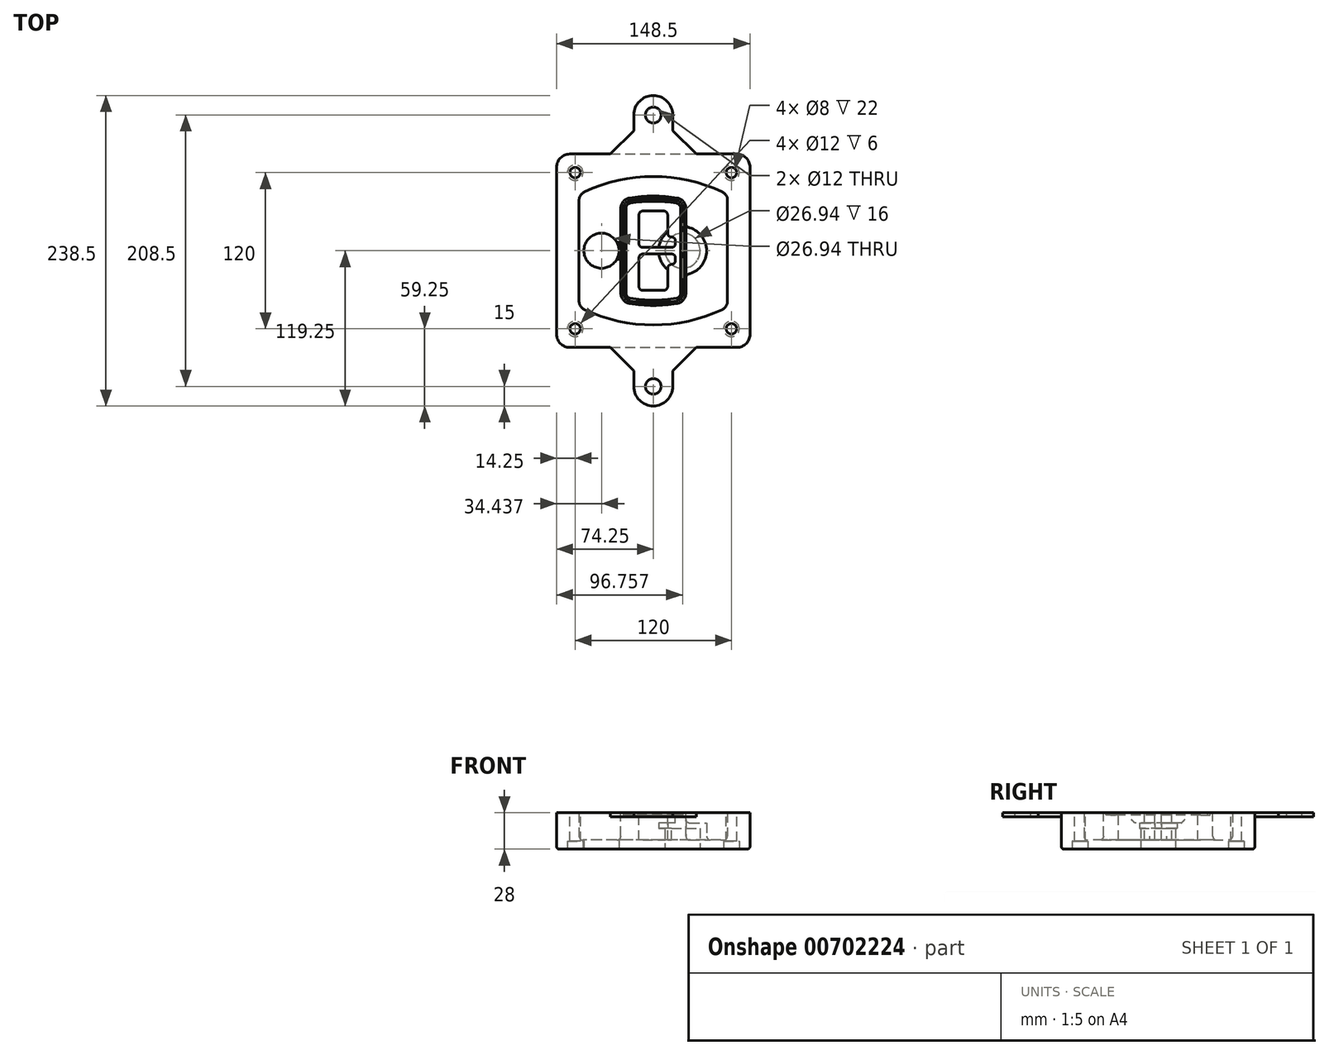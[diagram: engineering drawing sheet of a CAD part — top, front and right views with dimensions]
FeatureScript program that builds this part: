
annotation { "Feature Type Name" : "Feature", "Feature Type Description" : "" }
export const myFeature = defineFeature(function(context is Context, id is Id, definition is map)
    precondition{}
    {
        {
            var Q0;
            Q0=qCreatedBy(makeId("Top.planeOp"),FACE);
            var sketch = newSketch(context, id + "F0", { "sketchPlane" : qUnion([Q0])});
            skPoint(sketch, "E0.rect.middle", {"position": v(0, 0) * mm});
            skLineSegment(sketch, "E1.bottom", {"start": v(-64.25, -74.25) * mm, "end": v(64.25, -74.25) * mm});
            skLineSegment(sketch, "E1.top", {"start": v(-64.25, 74.25) * mm, "end": v(64.25, 74.25) * mm});
            skLineSegment(sketch, "E1.left", {"start": v(-74.25, -64.25) * mm, "end": v(-74.25, 64.25) * mm});
            skLineSegment(sketch, "E1.right", {"start": v(74.25, -64.25) * mm, "end": v(74.25, 64.25) * mm});
            skLineSegment(sketch, "E2", {"start": v(-74.25, 74.25) * mm, "end": v(74.25, -74.25) * mm, "construction": true});
            skLineSegment(sketch, "E3", {"start": v(74.25, 74.25) * mm, "end": v(-74.25, -74.25) * mm, "construction": true});
            skCircle(sketch, "E4", {"center": v(-60, 60) * mm, "radius": 4 * mm});
            skCircle(sketch, "E5", {"center": v(60, 60) * mm, "radius": 4 * mm});
            skCircle(sketch, "E6", {"center": v(60, -60) * mm, "radius": 4 * mm});
            skCircle(sketch, "E7", {"center": v(-60, -60) * mm, "radius": 4 * mm});
            skLineSegment(sketch, "E8", {"start": v(-60, 60) * mm, "end": v(60, 60) * mm, "construction": true});
            skLineSegment(sketch, "E9", {"start": v(60, 60) * mm, "end": v(60, -60) * mm, "construction": true});
            skLineSegment(sketch, "E10", {"start": v(60, -60) * mm, "end": v(-60, -60) * mm, "construction": true});
            skLineSegment(sketch, "E11", {"start": v(-60, -60) * mm, "end": v(-60, 60) * mm, "construction": true});
            skLineSegment(sketch, "E12", {"start": v(-60, 38.83) * mm, "end": v(-60, -38.83) * mm});
            skLineSegment(sketch, "E13", {"start": v(60, 38.83) * mm, "end": v(60, -38.83) * mm});
            skArc(sketch, "E14", {"start": v(54.26, 47.88) * mm, "mid": v(0, 60) * mm, "end": v(-54.26, 47.88) * mm});
            skArc(sketch, "E15", {"start": v(-54.26, -47.88) * mm, "mid": v(0, -60) * mm, "end": v(54.26, -47.88) * mm});
            skLineSegment(sketch, "E16", {"start": v(-60, 0) * mm, "end": v(60, 0) * mm, "construction": true});
            skPoint(sketch, "E17.visualSharp", {"position": v(-60, -45) * mm});
            skArc(sketch, "E17.filletArc", {"start": v(-60, -38.83) * mm, "mid": v(-58.44, -44.2) * mm, "end": v(-54.26, -47.88) * mm});
            skPoint(sketch, "E18.visualSharp", {"position": v(-60, 45) * mm});
            skArc(sketch, "E18.filletArc", {"start": v(-54.26, 47.88) * mm, "mid": v(-58.44, 44.2) * mm, "end": v(-60, 38.83) * mm});
            skPoint(sketch, "E19.visualSharp", {"position": v(60, 45) * mm});
            skArc(sketch, "E19.filletArc", {"start": v(60, 38.83) * mm, "mid": v(58.44, 44.2) * mm, "end": v(54.26, 47.88) * mm});
            skPoint(sketch, "E20.visualSharp", {"position": v(60, -45) * mm});
            skArc(sketch, "E20.filletArc", {"start": v(54.26, -47.88) * mm, "mid": v(58.44, -44.2) * mm, "end": v(60, -38.83) * mm});
            skPoint(sketch, "E21.visualSharp", {"position": v(-74.25, 74.25) * mm});
            skArc(sketch, "E21.filletArc", {"start": v(-64.25, 74.25) * mm, "mid": v(-71.32, 71.32) * mm, "end": v(-74.25, 64.25) * mm});
            skPoint(sketch, "E22.visualSharp", {"position": v(74.25, 74.25) * mm});
            skArc(sketch, "E22.filletArc", {"start": v(74.25, 64.25) * mm, "mid": v(71.32, 71.32) * mm, "end": v(64.25, 74.25) * mm});
            skPoint(sketch, "E23.visualSharp", {"position": v(74.25, -74.25) * mm});
            skArc(sketch, "E23.filletArc", {"start": v(64.25, -74.25) * mm, "mid": v(71.32, -71.32) * mm, "end": v(74.25, -64.25) * mm});
            skPoint(sketch, "E24.visualSharp", {"position": v(-74.25, -74.25) * mm});
            skArc(sketch, "E24.filletArc", {"start": v(-74.25, -64.25) * mm, "mid": v(-71.32, -71.32) * mm, "end": v(-64.25, -74.25) * mm});
            skArc(sketch, "E25.0", {"start": v(57, 38.83) * mm, "mid": v(55.9, 42.58) * mm, "end": v(52.98, 45.17) * mm});
            skLineSegment(sketch, "E25.1", {"start": v(57, 38.83) * mm, "end": v(57, -38.83) * mm});
            skArc(sketch, "E25.2", {"start": v(52.98, -45.17) * mm, "mid": v(55.9, -42.58) * mm, "end": v(57, -38.83) * mm});
            skArc(sketch, "E25.3", {"start": v(-52.98, -45.17) * mm, "mid": v(0, -57) * mm, "end": v(52.98, -45.17) * mm});
            skArc(sketch, "E25.4", {"start": v(-57, -38.83) * mm, "mid": v(-55.9, -42.58) * mm, "end": v(-52.98, -45.17) * mm});
            skArc(sketch, "E25.5", {"start": v(52.98, 45.17) * mm, "mid": v(0, 57) * mm, "end": v(-52.98, 45.17) * mm});
            skLineSegment(sketch, "E25.6", {"start": v(-57, 38.83) * mm, "end": v(-57, -38.83) * mm});
            skArc(sketch, "E25.7", {"start": v(-52.98, 45.17) * mm, "mid": v(-55.9, 42.58) * mm, "end": v(-57, 38.83) * mm});
            skArc(sketch, "E26.0", {"start": v(-55.96, 51.5) * mm, "mid": v(-61.82, 46.33) * mm, "end": v(-64, 38.83) * mm});
            skArc(sketch, "E26.1", {"start": v(55.96, 51.5) * mm, "mid": v(0, 64) * mm, "end": v(-55.96, 51.5) * mm});
            skArc(sketch, "E26.2", {"start": v(64, 38.83) * mm, "mid": v(61.82, 46.33) * mm, "end": v(55.96, 51.5) * mm});
            skLineSegment(sketch, "E26.3", {"start": v(64, 38.83) * mm, "end": v(64, -38.83) * mm});
            skArc(sketch, "E26.4", {"start": v(55.96, -51.5) * mm, "mid": v(61.82, -46.33) * mm, "end": v(64, -38.83) * mm});
            skLineSegment(sketch, "E26.5", {"start": v(-64, 38.83) * mm, "end": v(-64, -38.83) * mm});
            skArc(sketch, "E26.6", {"start": v(-55.96, -51.5) * mm, "mid": v(0, -64) * mm, "end": v(55.96, -51.5) * mm});
            skArc(sketch, "E26.7", {"start": v(-64, -38.83) * mm, "mid": v(-61.82, -46.33) * mm, "end": v(-55.96, -51.5) * mm});
            skSolve(sketch);
        }
        {
            var Q0;
            Q0=makeQuery(id+"F0.imprint","IMPRINT",FACE,{"disambiguationData":[TD([[makeQuery(id+"F0.imprint","IMPRINT",EDGE,{"derivedFrom":sQuery(id+"F0.wireOp",EDGE,"E1.bottom")}),1.0]])]});
            var Q1;
            Q1=makeQuery(id+"F0.imprint","IMPRINT",FACE,{"disambiguationData":[TD([[makeQuery(id+"F0.imprint","IMPRINT",EDGE,{"derivedFrom":sQuery(id+"F0.wireOp",EDGE,"E12")}),1.0]])]});
            var Q2;
            Q2=makeQuery(id+"F0.imprint","IMPRINT",FACE,{"disambiguationData":[TD([[makeQuery(id+"F0.imprint","IMPRINT",EDGE,{"derivedFrom":sQuery(id+"F0.wireOp",EDGE,"E25.0")}),1.0]])]});
            var Q3;
            Q3=makeQuery(id+"F0.imprint","IMPRINT",FACE,{"disambiguationData":[TD([[makeQuery(id+"F0.imprint","IMPRINT",EDGE,{"derivedFrom":sQuery(id+"F0.wireOp",EDGE,"E12")}),-1.0]])]});
            extrude(context, id + "F1", {"entities" : qUnion([Q0, Q1, Q2, Q3]), "oppositeDirection" : true, "depth" : 25 * mm});
        }
        {
            var Q0;
            Q0=makeQuery(id+"F0.imprint","IMPRINT",FACE,{"disambiguationData":[TD([[makeQuery(id+"F0.imprint","IMPRINT",EDGE,{"derivedFrom":sQuery(id+"F0.wireOp",EDGE,"E12")}),1.0]])]});
            extrude(context, id + "F2", {"entities" : qUnion([Q0]), "operationType" : NewBodyOperationType.ADD, "depth" : 3 * mm});
        }
        {
            var Q0;
            Q0=makeQuery(id+"F0.imprint","IMPRINT",FACE,{"disambiguationData":[TD([[makeQuery(id+"F0.imprint","IMPRINT",EDGE,{"derivedFrom":sQuery(id+"F0.wireOp",EDGE,"E25.0")}),1.0]])]});
            extrude(context, id + "F3", {"entities" : qUnion([Q0]), "operationType" : NewBodyOperationType.REMOVE, "oppositeDirection" : true, "depth" : 18 * mm});
        }
        {
            var Q0;
            Q0=makeQuery(id+"F2.opExtrude","CAP_FACE",FACE,{"disambiguationData":[OSD([sQuery(id+"F0.wireOp",EDGE,"E12"),sQuery(id+"F0.wireOp",EDGE,"E13"),sQuery(id+"F0.wireOp",EDGE,"E14"),sQuery(id+"F0.wireOp",EDGE,"E15"),sQuery(id+"F0.wireOp",EDGE,"E17.filletArc"),sQuery(id+"F0.wireOp",EDGE,"E18.filletArc"),sQuery(id+"F0.wireOp",EDGE,"E19.filletArc"),sQuery(id+"F0.wireOp",EDGE,"E20.filletArc"),sQuery(id+"F0.wireOp",EDGE,"E25.0"),sQuery(id+"F0.wireOp",EDGE,"E25.1"),sQuery(id+"F0.wireOp",EDGE,"E25.2"),sQuery(id+"F0.wireOp",EDGE,"E25.3"),sQuery(id+"F0.wireOp",EDGE,"E25.4"),sQuery(id+"F0.wireOp",EDGE,"E25.5"),sQuery(id+"F0.wireOp",EDGE,"E25.6"),sQuery(id+"F0.wireOp",EDGE,"E25.7")])],"isStart":false});
            var sketch = newSketch(context, id + "F4", { "sketchPlane" : qUnion([Q0])});
            skArc(sketch, "E27.0", {"start": v(-18.34, -40.45) * mm, "mid": v(0, -42) * mm, "end": v(18.34, -40.45) * mm});
            skArc(sketch, "E28.0", {"start": v(18.34, 40.45) * mm, "mid": v(0, 42) * mm, "end": v(-18.34, 40.45) * mm});
            skLineSegment(sketch, "E29", {"start": v(-25, 32.57) * mm, "end": v(-25, -32.57) * mm});
            skLineSegment(sketch, "E30", {"start": v(25, 32.57) * mm, "end": v(25, -32.57) * mm});
            skLineSegment(sketch, "E31", {"start": v(-25, 39.1) * mm, "end": v(25, 39.1) * mm, "construction": true});
            skLineSegment(sketch, "E32", {"start": v(-25, -39.1) * mm, "end": v(25, -39.1) * mm, "construction": true});
            skPoint(sketch, "E33.visualSharp", {"position": v(-25, 39.1) * mm});
            skArc(sketch, "E33.filletArc", {"start": v(-18.34, 40.45) * mm, "mid": v(-23.11, 37.73) * mm, "end": v(-25, 32.57) * mm});
            skPoint(sketch, "E34.visualSharp", {"position": v(25, 39.1) * mm});
            skArc(sketch, "E34.filletArc", {"start": v(25, 32.57) * mm, "mid": v(23.11, 37.73) * mm, "end": v(18.34, 40.45) * mm});
            skPoint(sketch, "E35.visualSharp", {"position": v(25, -39.1) * mm});
            skArc(sketch, "E35.filletArc", {"start": v(18.34, -40.45) * mm, "mid": v(23.11, -37.73) * mm, "end": v(25, -32.57) * mm});
            skPoint(sketch, "E36.visualSharp", {"position": v(-25, -39.1) * mm});
            skArc(sketch, "E36.filletArc", {"start": v(-25, -32.57) * mm, "mid": v(-23.11, -37.73) * mm, "end": v(-18.34, -40.45) * mm});
            skArc(sketch, "E37.0", {"start": v(52.98, 45.17) * mm, "mid": v(0, 57) * mm, "end": v(-52.98, 45.17) * mm});
            skArc(sketch, "E37.1", {"start": v(-52.98, 45.17) * mm, "mid": v(-55.9, 42.58) * mm, "end": v(-57, 38.83) * mm});
            skLineSegment(sketch, "E37.2", {"start": v(-57, 38.83) * mm, "end": v(-57, -38.83) * mm});
            skArc(sketch, "E37.3", {"start": v(-57, -38.83) * mm, "mid": v(-55.9, -42.58) * mm, "end": v(-52.98, -45.17) * mm});
            skArc(sketch, "E37.4", {"start": v(-52.98, -45.17) * mm, "mid": v(0, -57) * mm, "end": v(52.98, -45.17) * mm});
            skArc(sketch, "E37.5", {"start": v(52.98, -45.17) * mm, "mid": v(55.9, -42.58) * mm, "end": v(57, -38.83) * mm});
            skLineSegment(sketch, "E37.6", {"start": v(57, 38.83) * mm, "end": v(57, -38.83) * mm});
            skArc(sketch, "E37.7", {"start": v(57, 38.83) * mm, "mid": v(55.9, 42.58) * mm, "end": v(52.98, 45.17) * mm});
            skLineSegment(sketch, "E38.0", {"start": v(23, 32.57) * mm, "end": v(23, -32.57) * mm});
            skArc(sketch, "E38.1", {"start": v(18, -38.48) * mm, "mid": v(21.58, -36.44) * mm, "end": v(23, -32.57) * mm});
            skArc(sketch, "E38.2", {"start": v(-18, -38.48) * mm, "mid": v(0, -40) * mm, "end": v(18, -38.48) * mm});
            skArc(sketch, "E38.3", {"start": v(-23, -32.57) * mm, "mid": v(-21.58, -36.44) * mm, "end": v(-18, -38.48) * mm});
            skLineSegment(sketch, "E38.4", {"start": v(-23, 32.57) * mm, "end": v(-23, -32.57) * mm});
            skArc(sketch, "E38.5", {"start": v(23, 32.57) * mm, "mid": v(21.58, 36.44) * mm, "end": v(18, 38.48) * mm});
            skArc(sketch, "E38.6", {"start": v(-18, 38.48) * mm, "mid": v(-21.58, 36.44) * mm, "end": v(-23, 32.57) * mm});
            skArc(sketch, "E38.7", {"start": v(18, 38.48) * mm, "mid": v(0, 40) * mm, "end": v(-18, 38.48) * mm});
            skArc(sketch, "E39.0", {"start": v(21, 32.57) * mm, "mid": v(20.06, 35.15) * mm, "end": v(17.67, 36.5) * mm});
            skLineSegment(sketch, "E39.1", {"start": v(21, 32.57) * mm, "end": v(21, -32.57) * mm});
            skArc(sketch, "E39.2", {"start": v(17.67, -36.5) * mm, "mid": v(20.06, -35.15) * mm, "end": v(21, -32.57) * mm});
            skArc(sketch, "E39.3", {"start": v(-17.67, -36.5) * mm, "mid": v(0, -38) * mm, "end": v(17.67, -36.5) * mm});
            skArc(sketch, "E39.4", {"start": v(-21, -32.57) * mm, "mid": v(-20.06, -35.15) * mm, "end": v(-17.67, -36.5) * mm});
            skArc(sketch, "E39.5", {"start": v(17.67, 36.5) * mm, "mid": v(0, 38) * mm, "end": v(-17.67, 36.5) * mm});
            skLineSegment(sketch, "E39.6", {"start": v(-21, 32.57) * mm, "end": v(-21, -32.57) * mm});
            skArc(sketch, "E39.7", {"start": v(-17.67, 36.5) * mm, "mid": v(-20.06, 35.15) * mm, "end": v(-21, 32.57) * mm});
            skLineSegment(sketch, "E40", {"start": v(-25, 0) * mm, "end": v(25, 0) * mm, "construction": true});
            skLineSegment(sketch, "E41", {"start": v(-11, 5.5) * mm, "end": v(-11, 27.5) * mm});
            skLineSegment(sketch, "E42", {"start": v(-8, 30.5) * mm, "end": v(8, 30.5) * mm});
            skLineSegment(sketch, "E43", {"start": v(11, 27.5) * mm, "end": v(11, 13.5) * mm});
            skLineSegment(sketch, "E44", {"start": v(14, 10.5) * mm, "end": v(14, 10.5) * mm});
            skLineSegment(sketch, "E45", {"start": v(17, 7.5) * mm, "end": v(17, 5.5) * mm});
            skLineSegment(sketch, "E46", {"start": v(14, 2.5) * mm, "end": v(-8, 2.5) * mm});
            skPoint(sketch, "E47.visualSharp", {"position": v(-11, 30.5) * mm});
            skArc(sketch, "E47.filletArc", {"start": v(-8, 30.5) * mm, "mid": v(-10.12, 29.62) * mm, "end": v(-11, 27.5) * mm});
            skPoint(sketch, "E48.visualSharp", {"position": v(11, 30.5) * mm});
            skArc(sketch, "E48.filletArc", {"start": v(11, 27.5) * mm, "mid": v(10.12, 29.62) * mm, "end": v(8, 30.5) * mm});
            skPoint(sketch, "E49.visualSharp", {"position": v(11, 10.5) * mm});
            skArc(sketch, "E49.filletArc", {"start": v(11, 13.5) * mm, "mid": v(11.88, 11.38) * mm, "end": v(14, 10.5) * mm});
            skPoint(sketch, "E50.visualSharp", {"position": v(17, 10.5) * mm});
            skArc(sketch, "E50.filletArc", {"start": v(17, 7.5) * mm, "mid": v(16.12, 9.62) * mm, "end": v(14, 10.5) * mm});
            skPoint(sketch, "E51.visualSharp", {"position": v(17, 2.5) * mm});
            skArc(sketch, "E51.filletArc", {"start": v(14, 2.5) * mm, "mid": v(16.12, 3.38) * mm, "end": v(17, 5.5) * mm});
            skPoint(sketch, "E52.visualSharp", {"position": v(-11, 2.5) * mm});
            skArc(sketch, "E52.filletArc", {"start": v(-11, 5.5) * mm, "mid": v(-10.12, 3.38) * mm, "end": v(-8, 2.5) * mm});
            skLineSegment(sketch, "E53.0.MirrorCS", {"start": v(14, -2.5) * mm, "end": v(-8, -2.5) * mm});
            skArc(sketch, "E54.0.MirrorCS", {"start": v(-11, -5.5) * mm, "mid": v(-10.12, -3.38) * mm, "end": v(-8, -2.5) * mm});
            skLineSegment(sketch, "E55.0.MirrorCS", {"start": v(-11, -5.5) * mm, "end": v(-11, -27.5) * mm});
            skArc(sketch, "E56.0.MirrorCS", {"start": v(-8, -30.5) * mm, "mid": v(-10.12, -29.62) * mm, "end": v(-11, -27.5) * mm});
            skLineSegment(sketch, "E57.0.MirrorCS", {"start": v(-8, -30.5) * mm, "end": v(8, -30.5) * mm});
            skArc(sketch, "E58.0.MirrorCS", {"start": v(11, -27.5) * mm, "mid": v(10.12, -29.62) * mm, "end": v(8, -30.5) * mm});
            skLineSegment(sketch, "E59.0.MirrorCS", {"start": v(11, -27.5) * mm, "end": v(11, -13.5) * mm});
            skArc(sketch, "E60.0.MirrorCS", {"start": v(11, -13.5) * mm, "mid": v(11.88, -11.38) * mm, "end": v(14, -10.5) * mm});
            skArc(sketch, "E61.0.MirrorCS", {"start": v(17, -7.5) * mm, "mid": v(16.12, -9.62) * mm, "end": v(14, -10.5) * mm});
            skLineSegment(sketch, "E62.0.MirrorCS", {"start": v(17, -7.5) * mm, "end": v(17, -5.5) * mm});
            skArc(sketch, "E63.0.MirrorCS", {"start": v(14, -2.5) * mm, "mid": v(16.12, -3.38) * mm, "end": v(17, -5.5) * mm});
            skSolve(sketch);
        }
        {
            var Q0;
            Q0=makeQuery(id+"F4.imprint","IMPRINT",FACE,{"disambiguationData":[TD([[makeQuery(id+"F4.imprint","IMPRINT",EDGE,{"derivedFrom":sQuery(id+"F4.wireOp",EDGE,"E27.0")}),1.0]])]});
            var Q1;
            Q1=makeQuery(id+"F4.imprint","IMPRINT",FACE,{"disambiguationData":[TD([[makeQuery(id+"F4.imprint","IMPRINT",EDGE,{"derivedFrom":sQuery(id+"F4.wireOp",EDGE,"E38.0")}),-1.0]])]});
            var Q2;
            Q2=makeQuery(id+"F4.imprint","IMPRINT",FACE,{"disambiguationData":[TD([[makeQuery(id+"F4.imprint","IMPRINT",EDGE,{"derivedFrom":sQuery(id+"F4.wireOp",EDGE,"E39.0")}),1.0]])]});
            extrude(context, id + "F5", {"entities" : qUnion([Q0, Q1, Q2]), "operationType" : NewBodyOperationType.ADD, "endBound" : BoundingType.UP_TO_NEXT, "oppositeDirection" : true, "depth" : 25 * mm});
        }
        {
            var Q0;
            Q0=makeQuery(id+"F4.imprint","IMPRINT",FACE,{"disambiguationData":[TD([[makeQuery(id+"F4.imprint","IMPRINT",EDGE,{"derivedFrom":sQuery(id+"F4.wireOp",EDGE,"E38.0")}),-1.0]])]});
            extrude(context, id + "F6", {"entities" : qUnion([Q0]), "operationType" : NewBodyOperationType.REMOVE, "oppositeDirection" : true, "depth" : 2 * mm});
        }
        {
            var Q0;
            Q0=makeQuery(id+"F1.opExtrude","CAP_FACE",FACE,{"disambiguationData":[OSD([sQuery(id+"F0.wireOp",EDGE,"E1.bottom"),sQuery(id+"F0.wireOp",EDGE,"E1.top"),sQuery(id+"F0.wireOp",EDGE,"E1.left"),sQuery(id+"F0.wireOp",EDGE,"E1.right"),sQuery(id+"F0.wireOp",EDGE,"E4"),sQuery(id+"F0.wireOp",EDGE,"E5"),sQuery(id+"F0.wireOp",EDGE,"E6"),sQuery(id+"F0.wireOp",EDGE,"E7"),sQuery(id+"F0.wireOp",EDGE,"E21.filletArc"),sQuery(id+"F0.wireOp",EDGE,"E22.filletArc"),sQuery(id+"F0.wireOp",EDGE,"E23.filletArc"),sQuery(id+"F0.wireOp",EDGE,"E24.filletArc")])],"isStart":false});
            var sketch = newSketch(context, id + "F7", { "sketchPlane" : qUnion([Q0])});
            skCircle(sketch, "E64", {"center": v(22.5, 0) * mm, "radius": 13.47 * mm});
            skCircle(sketch, "E65", {"center": v(-39.81, 0) * mm, "radius": 13.47 * mm});
            skLineSegment(sketch, "E66", {"start": v(74.25, 0) * mm, "end": v(-74.25, 0) * mm});
            skCircle(sketch, "E67", {"center": v(22.5, 0) * mm, "radius": 18.47 * mm});
            skCircle(sketch, "E68", {"center": v(60, -60) * mm, "radius": 6 * mm});
            skCircle(sketch, "E69", {"center": v(-60, -60) * mm, "radius": 6 * mm});
            skCircle(sketch, "E70", {"center": v(-60, 60) * mm, "radius": 6 * mm});
            skCircle(sketch, "E71", {"center": v(60, 60) * mm, "radius": 6 * mm});
            skSolve(sketch);
        }
        {
            var Q0;
            {var subQ1=sQuery(id+"F7.wireOp",EDGE,"E66");var subQ4=sQuery(id+"F7.wireOp",EDGE,"E64");var subQ6=makeQuery(id+"F7.imprint","INTERSECT",VERTEX,{"disambiguationData":[OD(0.0)],"derivedFrom":[subQ4,subQ1]});Q0=makeQuery(id+"F7.imprint","IMPRINT",FACE,{"disambiguationData":[TD([[makeQuery(id+"F7.imprint","IMPRINT",EDGE,{"disambiguationData":[TD([[subQ6,-1.0]])],"derivedFrom":subQ4}),-1.0]])]});}
            var Q1;
            {var subQ0=sQuery(id+"F7.wireOp",EDGE,"E66");var subQ1=sQuery(id+"F7.wireOp",EDGE,"E64");var subQ3=makeQuery(id+"F7.imprint","INTERSECT",VERTEX,{"disambiguationData":[OD(0.0)],"derivedFrom":[subQ1,subQ0]});Q1=makeQuery(id+"F7.imprint","IMPRINT",FACE,{"disambiguationData":[TD([[makeQuery(id+"F7.imprint","IMPRINT",EDGE,{"disambiguationData":[TD([[subQ3,-1.0]])],"derivedFrom":subQ1}),1.0]])]});}
            var Q2;
            {var subQ0=sQuery(id+"F7.wireOp",EDGE,"E66");var subQ1=sQuery(id+"F7.wireOp",EDGE,"E64");var subQ3=makeQuery(id+"F7.imprint","INTERSECT",VERTEX,{"disambiguationData":[OD(0.0)],"derivedFrom":[subQ1,subQ0]});Q2=makeQuery(id+"F7.imprint","IMPRINT",FACE,{"disambiguationData":[TD([[makeQuery(id+"F7.imprint","IMPRINT",EDGE,{"disambiguationData":[TD([[subQ3,1.0]])],"derivedFrom":subQ1}),1.0]])]});}
            var Q3;
            {var subQ1=sQuery(id+"F7.wireOp",EDGE,"E66");var subQ4=sQuery(id+"F7.wireOp",EDGE,"E64");var subQ6=makeQuery(id+"F7.imprint","INTERSECT",VERTEX,{"disambiguationData":[OD(0.0)],"derivedFrom":[subQ4,subQ1]});Q3=makeQuery(id+"F7.imprint","IMPRINT",FACE,{"disambiguationData":[TD([[makeQuery(id+"F7.imprint","IMPRINT",EDGE,{"disambiguationData":[TD([[subQ6,1.0]])],"derivedFrom":subQ4}),-1.0]])]});}
            extrude(context, id + "F8", {"entities" : qUnion([Q0, Q1, Q2, Q3]), "operationType" : NewBodyOperationType.ADD, "oppositeDirection" : true, "depth" : 20 * mm});
        }
        {
            var Q0;
            {var subQ0=sQuery(id+"F7.wireOp",EDGE,"E66");var subQ1=sQuery(id+"F7.wireOp",EDGE,"E64");var subQ3=makeQuery(id+"F7.imprint","INTERSECT",VERTEX,{"disambiguationData":[OD(0.0)],"derivedFrom":[subQ1,subQ0]});Q0=makeQuery(id+"F7.imprint","IMPRINT",FACE,{"disambiguationData":[TD([[makeQuery(id+"F7.imprint","IMPRINT",EDGE,{"disambiguationData":[TD([[subQ3,-1.0]])],"derivedFrom":subQ1}),1.0]])]});}
            var Q1;
            {var subQ0=sQuery(id+"F7.wireOp",EDGE,"E66");var subQ1=sQuery(id+"F7.wireOp",EDGE,"E64");var subQ3=makeQuery(id+"F7.imprint","INTERSECT",VERTEX,{"disambiguationData":[OD(0.0)],"derivedFrom":[subQ1,subQ0]});Q1=makeQuery(id+"F7.imprint","IMPRINT",FACE,{"disambiguationData":[TD([[makeQuery(id+"F7.imprint","IMPRINT",EDGE,{"disambiguationData":[TD([[subQ3,1.0]])],"derivedFrom":subQ1}),1.0]])]});}
            extrude(context, id + "F9", {"entities" : qUnion([Q0, Q1]), "operationType" : NewBodyOperationType.REMOVE, "oppositeDirection" : true, "depth" : 16 * mm});
        }
        {
            var Q0;
            {var subQ0=sQuery(id+"F7.wireOp",EDGE,"E66");var subQ1=sQuery(id+"F7.wireOp",EDGE,"E65");var subQ3=makeQuery(id+"F7.imprint","INTERSECT",VERTEX,{"disambiguationData":[OD(0.0)],"derivedFrom":[subQ1,subQ0]});Q0=makeQuery(id+"F7.imprint","IMPRINT",FACE,{"disambiguationData":[TD([[makeQuery(id+"F7.imprint","IMPRINT",EDGE,{"disambiguationData":[TD([[subQ3,-1.0]])],"derivedFrom":subQ1}),1.0]])]});}
            var Q1;
            {var subQ0=sQuery(id+"F7.wireOp",EDGE,"E66");var subQ1=sQuery(id+"F7.wireOp",EDGE,"E65");var subQ3=makeQuery(id+"F7.imprint","INTERSECT",VERTEX,{"disambiguationData":[OD(0.0)],"derivedFrom":[subQ1,subQ0]});Q1=makeQuery(id+"F7.imprint","IMPRINT",FACE,{"disambiguationData":[TD([[makeQuery(id+"F7.imprint","IMPRINT",EDGE,{"disambiguationData":[TD([[subQ3,1.0]])],"derivedFrom":subQ1}),1.0]])]});}
            extrude(context, id + "F10", {"entities" : qUnion([Q0, Q1]), "operationType" : NewBodyOperationType.REMOVE, "oppositeDirection" : true, "depth" : 25 * mm});
        }
        {
            var Q0;
            Q0=makeQuery(id+"F7.imprint","IMPRINT",FACE,{"disambiguationData":[TD([[makeQuery(id+"F7.imprint","IMPRINT",EDGE,{"derivedFrom":sQuery(id+"F7.wireOp",EDGE,"E68")}),1.0]])]});
            var Q1;
            Q1=makeQuery(id+"F7.imprint","IMPRINT",FACE,{"disambiguationData":[TD([[makeQuery(id+"F7.imprint","IMPRINT",EDGE,{"derivedFrom":makeQuery(id+"F1.opExtrude","CAP_EDGE",EDGE,{"disambiguationData":[OSD([sQuery(id+"F0.wireOp",EDGE,"E5")])],"isStart":false})}),-1.0]])]});
            var Q2;
            Q2=makeQuery(id+"F7.imprint","IMPRINT",FACE,{"disambiguationData":[TD([[makeQuery(id+"F7.imprint","IMPRINT",EDGE,{"derivedFrom":sQuery(id+"F7.wireOp",EDGE,"E69")}),1.0]])]});
            var Q3;
            Q3=makeQuery(id+"F7.imprint","IMPRINT",FACE,{"disambiguationData":[TD([[makeQuery(id+"F7.imprint","IMPRINT",EDGE,{"derivedFrom":makeQuery(id+"F1.opExtrude","CAP_EDGE",EDGE,{"disambiguationData":[OSD([sQuery(id+"F0.wireOp",EDGE,"E4")])],"isStart":false})}),-1.0]])]});
            var Q4;
            Q4=makeQuery(id+"F7.imprint","IMPRINT",FACE,{"disambiguationData":[TD([[makeQuery(id+"F7.imprint","IMPRINT",EDGE,{"derivedFrom":sQuery(id+"F7.wireOp",EDGE,"E70")}),1.0]])]});
            var Q5;
            Q5=makeQuery(id+"F7.imprint","IMPRINT",FACE,{"disambiguationData":[TD([[makeQuery(id+"F7.imprint","IMPRINT",EDGE,{"derivedFrom":makeQuery(id+"F1.opExtrude","CAP_EDGE",EDGE,{"disambiguationData":[OSD([sQuery(id+"F0.wireOp",EDGE,"E7")])],"isStart":false})}),-1.0]])]});
            var Q6;
            Q6=makeQuery(id+"F7.imprint","IMPRINT",FACE,{"disambiguationData":[TD([[makeQuery(id+"F7.imprint","IMPRINT",EDGE,{"derivedFrom":sQuery(id+"F7.wireOp",EDGE,"E71")}),1.0]])]});
            var Q7;
            Q7=makeQuery(id+"F7.imprint","IMPRINT",FACE,{"disambiguationData":[TD([[makeQuery(id+"F7.imprint","IMPRINT",EDGE,{"derivedFrom":makeQuery(id+"F1.opExtrude","CAP_EDGE",EDGE,{"disambiguationData":[OSD([sQuery(id+"F0.wireOp",EDGE,"E6")])],"isStart":false})}),-1.0]])]});
            extrude(context, id + "F11", {"entities" : qUnion([Q0, Q1, Q2, Q3, Q4, Q5, Q6, Q7]), "operationType" : NewBodyOperationType.REMOVE, "oppositeDirection" : true, "depth" : 6 * mm});
        }
        {
            var Q0;
            Q0=makeQuery(id+"F9.boolean.opBoolean","COPY",FACE,{"derivedFrom":makeQuery(id+"F9.opExtrude","CAP_FACE",FACE,{"disambiguationData":[OSD([sQuery(id+"F7.wireOp",EDGE,"E64")])],"isStart":false})});
            var sketch = newSketch(context, id + "F12", { "sketchPlane" : qUnion([Q0])});
            skArc(sketch, "E72.0", {"start": v(11, 14.45) * mm, "mid": v(6.45, 9.13) * mm, "end": v(4.2, 2.5) * mm});
            skArc(sketch, "E72.1", {"start": v(4.2, -2.5) * mm, "mid": v(6.45, -9.13) * mm, "end": v(11, -14.45) * mm});
            skLineSegment(sketch, "E73", {"start": v(4.2, -2.5) * mm, "end": v(14, -2.5) * mm});
            skLineSegment(sketch, "E74.0", {"start": v(14, 2.5) * mm, "end": v(4.2, 2.5) * mm});
            skArc(sketch, "E74.1", {"start": v(14, 2.5) * mm, "mid": v(16.12, 3.38) * mm, "end": v(17, 5.5) * mm});
            skLineSegment(sketch, "E74.2", {"start": v(17, 7.5) * mm, "end": v(17, 5.5) * mm});
            skArc(sketch, "E74.3", {"start": v(17, 7.5) * mm, "mid": v(16.12, 9.62) * mm, "end": v(14, 10.5) * mm});
            skArc(sketch, "E74.4", {"start": v(11, 13.5) * mm, "mid": v(11.88, 11.38) * mm, "end": v(14, 10.5) * mm});
            skLineSegment(sketch, "E74.5", {"start": v(11, 14.45) * mm, "end": v(11, 13.5) * mm});
            skLineSegment(sketch, "E74.7", {"start": v(14, -2.5) * mm, "end": v(4.2, -2.5) * mm});
            skArc(sketch, "E74.8", {"start": v(14, -2.5) * mm, "mid": v(16.12, -3.38) * mm, "end": v(17, -5.5) * mm});
            skLineSegment(sketch, "E74.9", {"start": v(17, -7.5) * mm, "end": v(17, -5.5) * mm});
            skArc(sketch, "E74.10", {"start": v(17, -7.5) * mm, "mid": v(16.12, -9.62) * mm, "end": v(14, -10.5) * mm});
            skArc(sketch, "E74.11", {"start": v(11, -13.5) * mm, "mid": v(11.88, -11.38) * mm, "end": v(14, -10.5) * mm});
            skLineSegment(sketch, "E74.12", {"start": v(11, -14.45) * mm, "end": v(11, -13.5) * mm});
            skPoint(sketch, "E75.orphan", {"position": v(11, -27.5) * mm});
            skPoint(sketch, "E76.orphan", {"position": v(-8, -2.5) * mm});
            skPoint(sketch, "E77.orphan", {"position": v(-8, 2.5) * mm});
            skPoint(sketch, "E78.orphan", {"position": v(11, 27.5) * mm});
            skSolve(sketch);
        }
        {
            var Q0;
            {var subQ7=sQuery(id+"F12.wireOp",EDGE,"E72.0");var subQ14=sQuery(id+"F12.wireOp",EDGE,"E72.1");var subQ16=sQuery(id+"F12.wireOp",EDGE,"E74.1");var subQ18=sQuery(id+"F12.wireOp",EDGE,"E74.8");Q0=qUnion([makeQuery(id+"F12.imprint","IMPRINT",FACE,{"disambiguationData":[TD([[makeQuery(id+"F12.imprint","IMPRINT",EDGE,{"derivedFrom":subQ7}),1.0]])]}),makeQuery(id+"F12.imprint","IMPRINT",FACE,{"disambiguationData":[TD([[makeQuery(id+"F12.imprint","IMPRINT",EDGE,{"derivedFrom":subQ14}),1.0]])]}),makeQuery(id+"F12.imprint","IMPRINT",FACE,{"disambiguationData":[TD([[makeQuery(id+"F12.imprint","IMPRINT",EDGE,{"derivedFrom":subQ16}),1.0]])]}),makeQuery(id+"F12.imprint","IMPRINT",FACE,{"disambiguationData":[TD([[makeQuery(id+"F12.imprint","IMPRINT",EDGE,{"derivedFrom":subQ18}),-1.0]])]})]);}
            var Q1;
            Q1=makeQuery(id+"F5.boolean.opBoolean","SPLIT",FACE,{"disambiguationData":[TD([makeQuery(id+"F5.opExtrude","SWEPT_FACE",FACE,{"disambiguationData":[OSD([sQuery(id+"F4.wireOp",EDGE,"E41")])]})])],"derivedFrom":makeQuery(id+"F3.boolean.opBoolean","COPY",FACE,{"derivedFrom":makeQuery(id+"F3.opExtrude","CAP_FACE",FACE,{"disambiguationData":[OSD([sQuery(id+"F0.wireOp",EDGE,"E25.0"),sQuery(id+"F0.wireOp",EDGE,"E25.1"),sQuery(id+"F0.wireOp",EDGE,"E25.2"),sQuery(id+"F0.wireOp",EDGE,"E25.3"),sQuery(id+"F0.wireOp",EDGE,"E25.4"),sQuery(id+"F0.wireOp",EDGE,"E25.5"),sQuery(id+"F0.wireOp",EDGE,"E25.6"),sQuery(id+"F0.wireOp",EDGE,"E25.7")])],"isStart":false})})});
            extrude(context, id + "F13", {"entities" : qUnion([Q0]), "operationType" : NewBodyOperationType.REMOVE, "endBound" : BoundingType.UP_TO_SURFACE, "endBoundEntityFace" : qUnion([Q1]), "depth" : 25 * mm});
        }
        {
            var Q0;
            Q0=makeQuery(id+"F3.boolean.opBoolean","COPY",EDGE,{"derivedFrom":makeQuery(id+"F3.opExtrude","CAP_EDGE",EDGE,{"disambiguationData":[OSD([sQuery(id+"F0.wireOp",EDGE,"E25.6")])],"isStart":false})});
            var Q1;
            Q1=makeQuery(id+"F8.boolean.opBoolean","INTERSECT",EDGE,{"derivedFrom":[makeQuery(id+"F5.opExtrude","SWEPT_FACE",FACE,{"disambiguationData":[OSD([sQuery(id+"F4.wireOp",EDGE,"E30")])]}),makeQuery(id+"F8.opExtrude","CAP_FACE",FACE,{"disambiguationData":[OSD([sQuery(id+"F7.wireOp",EDGE,"E67")])],"isStart":false})]});
            var Q2;
            Q2=makeQuery(id+"F8.boolean.opBoolean","INTERSECT",EDGE,{"disambiguationData":[OD(1.0)],"derivedFrom":[makeQuery(id+"F5.opExtrude","SWEPT_FACE",FACE,{"disambiguationData":[OSD([sQuery(id+"F4.wireOp",EDGE,"E30")])]}),makeQuery(id+"F8.opExtrude","SWEPT_FACE",FACE,{"disambiguationData":[OSD([sQuery(id+"F7.wireOp",EDGE,"E67")])]})]});
            var Q3;
            {var subQ0=sQuery(id+"F4.wireOp",EDGE,"E30");Q3=makeQuery(id+"F8.boolean.opBoolean","SPLIT",EDGE,{"disambiguationData":[TD([makeQuery(id+"F5.opExtrude","SWEPT_FACE",FACE,{"disambiguationData":[OSD([sQuery(id+"F4.wireOp",EDGE,"E35.filletArc")])]})])],"derivedFrom":makeQuery(id+"F5.opExtrude","CAP_EDGE",EDGE,{"disambiguationData":[OSD([subQ0])],"isStart":false})});}
            var Q4;
            {var subQ0=sQuery(id+"F0.wireOp",EDGE,"E25.7");var subQ1=sQuery(id+"F0.wireOp",EDGE,"E25.1");var subQ2=sQuery(id+"F0.wireOp",EDGE,"E25.6");var subQ3=sQuery(id+"F0.wireOp",EDGE,"E25.5");var subQ4=sQuery(id+"F0.wireOp",EDGE,"E25.4");var subQ5=sQuery(id+"F0.wireOp",EDGE,"E25.0");var subQ6=sQuery(id+"F0.wireOp",EDGE,"E25.2");var subQ7=sQuery(id+"F0.wireOp",EDGE,"E25.3");Q4=makeQuery(id+"F8.boolean.opBoolean","INTERSECT",EDGE,{"derivedFrom":[makeQuery(id+"F5.boolean.opBoolean","SPLIT",FACE,{"disambiguationData":[TD([makeQuery(id+"F2.opExtrude","SWEPT_FACE",FACE,{"disambiguationData":[OSD([subQ5])]})])],"derivedFrom":makeQuery(id+"F3.boolean.opBoolean","COPY",FACE,{"derivedFrom":makeQuery(id+"F3.opExtrude","CAP_FACE",FACE,{"disambiguationData":[OSD([subQ5,subQ1,subQ6,subQ7,subQ4,subQ3,subQ2,subQ0])],"isStart":false})})}),makeQuery(id+"F8.opExtrude","SWEPT_FACE",FACE,{"disambiguationData":[OSD([sQuery(id+"F7.wireOp",EDGE,"E67")])]})]});}
            var Q5;
            Q5=makeQuery(id+"F8.boolean.opBoolean","INTERSECT",EDGE,{"disambiguationData":[OD(0.0)],"derivedFrom":[makeQuery(id+"F5.opExtrude","SWEPT_FACE",FACE,{"disambiguationData":[OSD([sQuery(id+"F4.wireOp",EDGE,"E30")])]}),makeQuery(id+"F8.opExtrude","SWEPT_FACE",FACE,{"disambiguationData":[OSD([sQuery(id+"F7.wireOp",EDGE,"E67")])]})]});
            fillet(context, id + "F14", {"entities" : qUnion([Q0, Q1, Q2, Q3, Q4, Q5]), "radius" : 3 * mm, "tangentPropagation" : true, "allowEdgeOverflow" : false});
        }
        {
            var Q0;
            Q0=makeQuery(id+"F1.opExtrude","CAP_EDGE",EDGE,{"disambiguationData":[OSD([sQuery(id+"F0.wireOp",EDGE,"E1.bottom")])],"isStart":false});
            fillet(context, id + "F15", {"entities" : qUnion([Q0]), "radius" : 2 * mm, "tangentPropagation" : true, "allowEdgeOverflow" : false});
        }
        {
            var Q0;
            {var subQ0=sQuery(id+"F0.wireOp",EDGE,"E21.filletArc");var subQ1=sQuery(id+"F0.wireOp",EDGE,"E7");var subQ2=sQuery(id+"F0.wireOp",EDGE,"E6");var subQ3=sQuery(id+"F0.wireOp",EDGE,"E5");var subQ4=sQuery(id+"F0.wireOp",EDGE,"E4");var subQ5=sQuery(id+"F0.wireOp",EDGE,"E22.filletArc");var subQ6=sQuery(id+"F0.wireOp",EDGE,"E1.bottom");var subQ7=sQuery(id+"F0.wireOp",EDGE,"E1.right");var subQ8=sQuery(id+"F0.wireOp",EDGE,"E1.top");var subQ9=sQuery(id+"F0.wireOp",EDGE,"E1.left");var subQ10=sQuery(id+"F0.wireOp",EDGE,"E23.filletArc");var subQ11=sQuery(id+"F0.wireOp",EDGE,"E24.filletArc");Q0=makeQuery(id+"F2.boolean.opBoolean","SPLIT",FACE,{"disambiguationData":[TD([makeQuery(id+"F1.opExtrude","SWEPT_FACE",FACE,{"disambiguationData":[OSD([subQ6])]})])],"derivedFrom":makeQuery(id+"F1.opExtrude","CAP_FACE",FACE,{"disambiguationData":[OSD([subQ6,subQ8,subQ9,subQ7,subQ4,subQ3,subQ2,subQ1,subQ0,subQ5,subQ10,subQ11])],"isStart":true})});}
            var sketch = newSketch(context, id + "F16", { "sketchPlane" : qUnion([Q0])});
            skCircle(sketch, "E79", {"center": v(0, 104.25) * mm, "radius": 6 * mm});
            skPoint(sketch, "E79.centerSnap0", {"position": v(0, 74.25) * mm});
            skArc(sketch, "E80", {"start": v(15, 104.25) * mm, "mid": v(0, 119.25) * mm, "end": v(-15, 104.25) * mm});
            skLineSegment(sketch, "E81", {"start": v(-15, 104.25) * mm, "end": v(-15, 92.25) * mm});
            skLineSegment(sketch, "E82", {"start": v(15, 104.25) * mm, "end": v(15, 92.25) * mm});
            skLineSegment(sketch, "E83", {"start": v(-15, 74.25) * mm, "end": v(-33, 74.25) * mm});
            skLineSegment(sketch, "E84", {"start": v(-33, 74.25) * mm, "end": v(-15, 92.25) * mm});
            skLineSegment(sketch, "E85", {"start": v(15, 74.25) * mm, "end": v(33, 74.25) * mm});
            skLineSegment(sketch, "E86", {"start": v(33, 74.25) * mm, "end": v(15, 92.25) * mm});
            skLineSegment(sketch, "E87.MirrorCS", {"start": v(-33, -74.25) * mm, "end": v(-15, -92.25) * mm});
            skLineSegment(sketch, "E88.MirrorCS", {"start": v(-15, -104.25) * mm, "end": v(-15, -92.25) * mm});
            skArc(sketch, "E89.MirrorCS", {"start": v(15, -104.25) * mm, "mid": v(0, -119.25) * mm, "end": v(-15, -104.25) * mm});
            skLineSegment(sketch, "E90.MirrorCS", {"start": v(15, -104.25) * mm, "end": v(15, -92.25) * mm});
            skCircle(sketch, "E91.MirrorC", {"center": v(0, -104.25) * mm, "radius": 6 * mm});
            skLineSegment(sketch, "E92.MirrorCS", {"start": v(33, -74.25) * mm, "end": v(15, -92.25) * mm});
            skSolve(sketch);
        }
        {
            var Q0;
            Q0=makeQuery(id+"F16.imprint","IMPRINT",FACE,{"disambiguationData":[TD([[makeQuery(id+"F16.imprint","IMPRINT",EDGE,{"derivedFrom":sQuery(id+"F16.wireOp",EDGE,"E79")}),-1.0]])]});
            var Q1;
            {var subQ0=sQuery(id+"F16.wireOp",EDGE,"E87.MirrorCS");Q1=makeQuery(id+"F16.imprint","IMPRINT",FACE,{"disambiguationData":[TD([[makeQuery(id+"F16.imprint","IMPRINT",EDGE,{"derivedFrom":subQ0}),1.0]])]});}
            var Q2;
            {var subQ5=sQuery(id+"F16.wireOp",EDGE,"E83");Q2=makeQuery(id+"F16.imprint","IMPRINT",FACE,{"disambiguationData":[TD([[makeQuery(id+"F16.imprint","IMPRINT",EDGE,{"derivedFrom":subQ5}),-1.0]])]});}
            var Q3;
            Q3=makeQuery(id+"F2.opExtrude","CAP_FACE",FACE,{"disambiguationData":[OSD([sQuery(id+"F0.wireOp",EDGE,"E12"),sQuery(id+"F0.wireOp",EDGE,"E13"),sQuery(id+"F0.wireOp",EDGE,"E14"),sQuery(id+"F0.wireOp",EDGE,"E15"),sQuery(id+"F0.wireOp",EDGE,"E17.filletArc"),sQuery(id+"F0.wireOp",EDGE,"E18.filletArc"),sQuery(id+"F0.wireOp",EDGE,"E19.filletArc"),sQuery(id+"F0.wireOp",EDGE,"E20.filletArc"),sQuery(id+"F0.wireOp",EDGE,"E25.0"),sQuery(id+"F0.wireOp",EDGE,"E25.1"),sQuery(id+"F0.wireOp",EDGE,"E25.2"),sQuery(id+"F0.wireOp",EDGE,"E25.3"),sQuery(id+"F0.wireOp",EDGE,"E25.4"),sQuery(id+"F0.wireOp",EDGE,"E25.5"),sQuery(id+"F0.wireOp",EDGE,"E25.6"),sQuery(id+"F0.wireOp",EDGE,"E25.7")])],"isStart":false});
            extrude(context, id + "F17", {"entities" : qUnion([Q0, Q1, Q2]), "operationType" : NewBodyOperationType.ADD, "endBound" : BoundingType.UP_TO_SURFACE, "depth" : 25 * mm, "endBoundEntityFace" : qUnion([Q3]), "offsetDistance" : 25 * mm});
        }
    });
